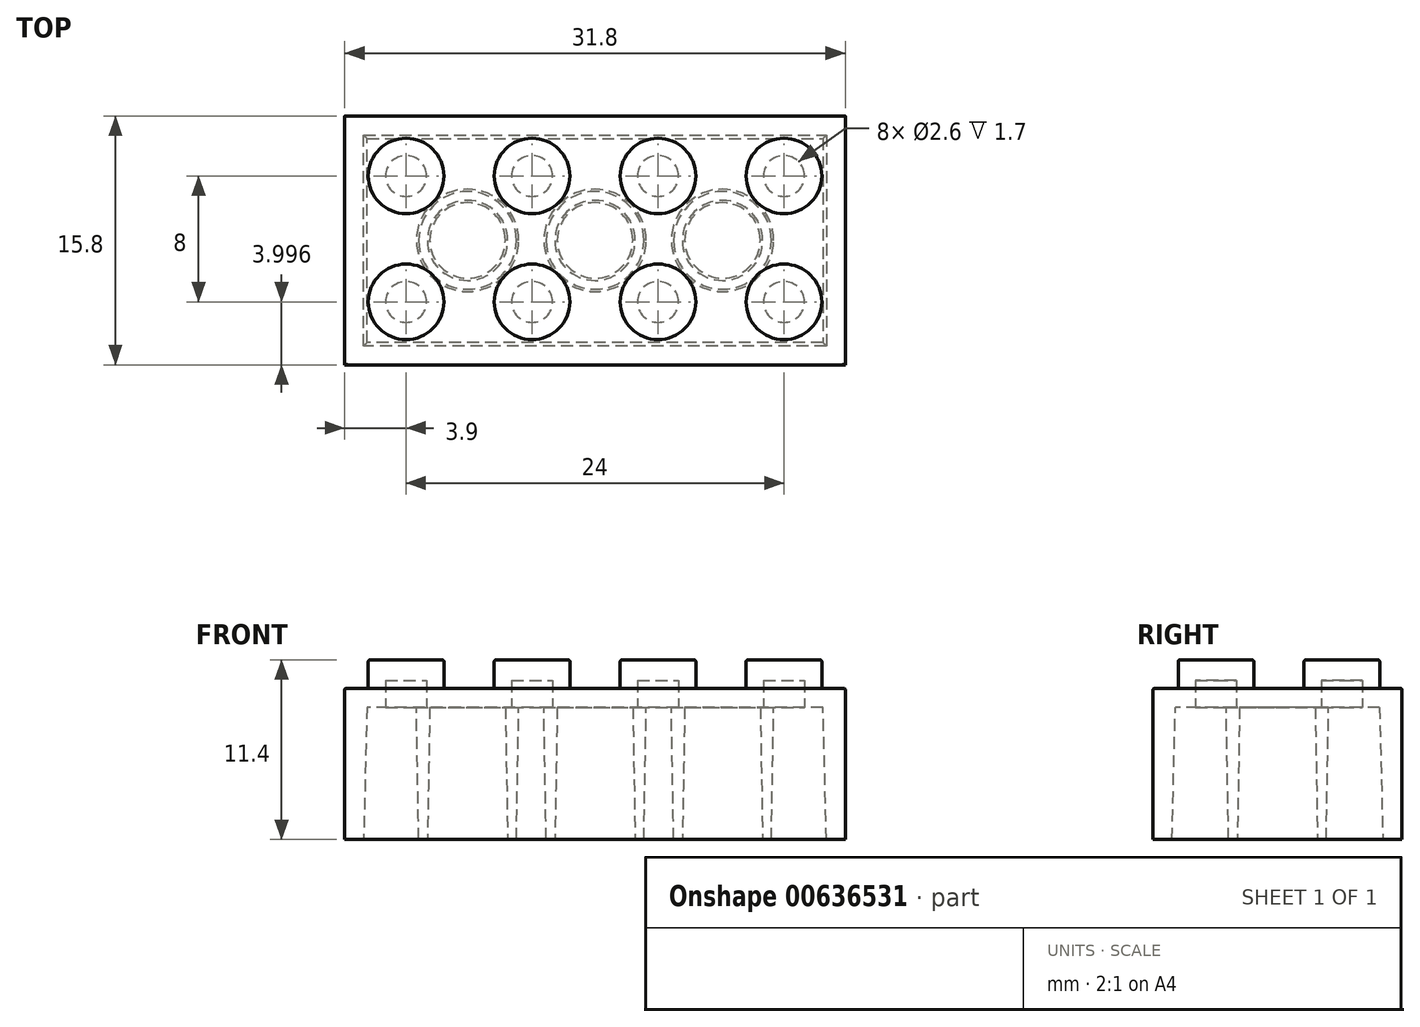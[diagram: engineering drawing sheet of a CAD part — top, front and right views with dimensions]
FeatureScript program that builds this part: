
annotation { "Feature Type Name" : "Feature", "Feature Type Description" : "" }
export const myFeature = defineFeature(function(context is Context, id is Id, definition is map)
    precondition{}
    {
        {
            var Q0;
            Q0=qCreatedBy(makeId("Top.planeOp"),FACE);
            var sketch = newSketch(context, id + "F0", { "sketchPlane" : qUnion([Q0])});
            skLineSegment(sketch, "E0.rect.bottom", {"start": v(15.9, -7.9) * mm, "end": v(-15.9, -7.9) * mm});
            skLineSegment(sketch, "E0.rect.top", {"start": v(15.9, 7.9) * mm, "end": v(-15.9, 7.9) * mm});
            skLineSegment(sketch, "E0.rect.left", {"start": v(15.9, -7.9) * mm, "end": v(15.9, 7.9) * mm});
            skLineSegment(sketch, "E0.rect.right", {"start": v(-15.9, -7.9) * mm, "end": v(-15.9, 7.9) * mm});
            skPoint(sketch, "E0.rect.middle", {"position": v(0, 0) * mm});
            skSolve(sketch);
        }
        {
            var Q0;
            Q0=makeQuery(id+"F0.imprint","IMPRINT",FACE,{"disambiguationData":[TD([[makeQuery(id+"F0.imprint","IMPRINT",EDGE,{"derivedFrom":sQuery(id+"F0.wireOp",EDGE,"E0.rect.bottom")}),-1.0]])]});
            extrude(context, id + "F1", {"entities" : qUnion([Q0]), "depth" : 9.6 * mm});
        }
        {
            var Q0;
            Q0=makeQuery(id+"F1.opExtrude","CAP_FACE",FACE,{"disambiguationData":[OSD([sQuery(id+"F0.wireOp",EDGE,"E0.rect.bottom"),sQuery(id+"F0.wireOp",EDGE,"E0.rect.top"),sQuery(id+"F0.wireOp",EDGE,"E0.rect.left"),sQuery(id+"F0.wireOp",EDGE,"E0.rect.right")])],"isStart":false});
            var sketch = newSketch(context, id + "F2", { "sketchPlane" : qUnion([Q0])});
            skCircle(sketch, "E1", {"center": v(12, -3.9) * mm, "radius": 2.4 * mm});
            skCircle(sketch, "E2.0.1.0", {"center": v(12, 4.1) * mm, "radius": 2.4 * mm});
            skCircle(sketch, "E2.1.0.0", {"center": v(4, -3.9) * mm, "radius": 2.4 * mm});
            skCircle(sketch, "E2.1.1.0", {"center": v(4, 4.1) * mm, "radius": 2.4 * mm});
            skCircle(sketch, "E2.2.0.0", {"center": v(-4, -3.9) * mm, "radius": 2.4 * mm});
            skCircle(sketch, "E2.2.1.0", {"center": v(-4, 4.1) * mm, "radius": 2.4 * mm});
            skCircle(sketch, "E2.3.0.0", {"center": v(-12, -3.9) * mm, "radius": 2.4 * mm});
            skCircle(sketch, "E2.3.1.0", {"center": v(-12, 4.1) * mm, "radius": 2.4 * mm});
            skLineSegment(sketch, "E2.direction1", {"start": v(12, -3.9) * mm, "end": v(4, -3.9) * mm, "construction": true});
            skLineSegment(sketch, "E2.direction2", {"start": v(12, -3.9) * mm, "end": v(12, 4.1) * mm, "construction": true});
            skSolve(sketch);
        }
        {
            var Q0;
            Q0=qSketchRegion(id+"F2",true);
            extrude(context, id + "F3", {"entities" : qUnion([Q0]), "operationType" : NewBodyOperationType.ADD, "depth" : 1.8 * mm});
        }
        {
            var Q0;
            Q0=makeQuery(id+"F1.opExtrude","CAP_FACE",FACE,{"disambiguationData":[OSD([sQuery(id+"F0.wireOp",EDGE,"E0.rect.bottom"),sQuery(id+"F0.wireOp",EDGE,"E0.rect.top"),sQuery(id+"F0.wireOp",EDGE,"E0.rect.left"),sQuery(id+"F0.wireOp",EDGE,"E0.rect.right")])],"isStart":true});
            var sketch = newSketch(context, id + "F4", { "sketchPlane" : qUnion([Q0])});
            skLineSegment(sketch, "E3.0", {"start": v(14.7, 6.7) * mm, "end": v(-14.7, 6.7) * mm});
            skLineSegment(sketch, "E3.1", {"start": v(14.7, 6.7) * mm, "end": v(14.7, -6.7) * mm});
            skLineSegment(sketch, "E3.2", {"start": v(14.7, -6.7) * mm, "end": v(-14.7, -6.7) * mm});
            skLineSegment(sketch, "E3.3", {"start": v(-14.7, 6.7) * mm, "end": v(-14.7, -6.7) * mm});
            skSolve(sketch);
        }
        {
            var Q0;
            Q0=qSketchRegion(id+"F4",true);
            extrude(context, id + "F5", {"entities" : qUnion([Q0]), "operationType" : NewBodyOperationType.REMOVE, "oppositeDirection" : true, "depth" : (9.6 - 1.2) * mm, "hasDraft" : true, "draftAngle" : 1.5 * degree, "draftPullDirection" : true});
        }
        {
            var Q0;
            Q0=makeQuery(id+"F5.boolean.opBoolean","COPY",FACE,{"derivedFrom":makeQuery(id+"F5.opExtrude","CAP_FACE",FACE,{"disambiguationData":[OSD([sQuery(id+"F4.wireOp",EDGE,"E3.0"),sQuery(id+"F4.wireOp",EDGE,"E3.1"),sQuery(id+"F4.wireOp",EDGE,"E3.2"),sQuery(id+"F4.wireOp",EDGE,"E3.3")])],"isStart":false})});
            var sketch = newSketch(context, id + "F6", { "sketchPlane" : qUnion([Q0])});
            skCircle(sketch, "E4.0", {"center": v(12, 3.9) * mm, "radius": 2.4 * mm, "construction": true});
            skCircle(sketch, "E5.0", {"center": v(4, 3.9) * mm, "radius": 2.4 * mm, "construction": true});
            skCircle(sketch, "E6.0", {"center": v(-4, 3.9) * mm, "radius": 2.4 * mm, "construction": true});
            skCircle(sketch, "E7.0", {"center": v(-12, 3.9) * mm, "radius": 2.4 * mm, "construction": true});
            skCircle(sketch, "E8.0", {"center": v(-12, -4.1) * mm, "radius": 2.4 * mm, "construction": true});
            skCircle(sketch, "E9.0", {"center": v(-4, -4.1) * mm, "radius": 2.4 * mm, "construction": true});
            skCircle(sketch, "E10.0", {"center": v(4, -4.1) * mm, "radius": 2.4 * mm, "construction": true});
            skCircle(sketch, "E11.0", {"center": v(12, -4.1) * mm, "radius": 2.4 * mm, "construction": true});
            skCircle(sketch, "E12", {"center": v(-12, 3.9) * mm, "radius": 1.3 * mm});
            skCircle(sketch, "E13", {"center": v(-4, 3.9) * mm, "radius": 1.3 * mm});
            skCircle(sketch, "E14", {"center": v(4, 3.9) * mm, "radius": 1.3 * mm});
            skCircle(sketch, "E15", {"center": v(12, 3.9) * mm, "radius": 1.3 * mm});
            skCircle(sketch, "E16", {"center": v(12, -4.1) * mm, "radius": 1.3 * mm});
            skCircle(sketch, "E17", {"center": v(4, -4.1) * mm, "radius": 1.3 * mm});
            skCircle(sketch, "E18", {"center": v(-4, -4.1) * mm, "radius": 1.3 * mm});
            skCircle(sketch, "E19", {"center": v(-12, -4.1) * mm, "radius": 1.3 * mm});
            skSolve(sketch);
        }
        {
            var Q0;
            Q0=qSketchRegion(id+"F6",true);
            extrude(context, id + "F7", {"entities" : qUnion([Q0]), "operationType" : NewBodyOperationType.REMOVE, "oppositeDirection" : true, "depth" : 1.7 * mm});
        }
        {
            var Q0;
            Q0=makeQuery(id+"F5.boolean.opBoolean","COPY",FACE,{"derivedFrom":makeQuery(id+"F5.opExtrude","CAP_FACE",FACE,{"disambiguationData":[OSD([sQuery(id+"F4.wireOp",EDGE,"E3.0"),sQuery(id+"F4.wireOp",EDGE,"E3.1"),sQuery(id+"F4.wireOp",EDGE,"E3.2"),sQuery(id+"F4.wireOp",EDGE,"E3.3")])],"isStart":false})});
            var sketch = newSketch(context, id + "F8", { "sketchPlane" : qUnion([Q0])});
            skLineSegment(sketch, "E20.0", {"start": v(-15.9, 7.9) * mm, "end": v(-15.9, -7.9) * mm, "construction": true});
            skLineSegment(sketch, "E21", {"start": v(-15.9, 0) * mm, "end": v(17.94, 0) * mm});
            skPoint(sketch, "E21.endSnap0", {"position": v(-15.9, 0) * mm});
            skCircle(sketch, "E22", {"center": v(0, 0) * mm, "radius": 3.25 * mm});
            skCircle(sketch, "E23", {"center": v(8.1, 0) * mm, "radius": 3.25 * mm});
            skCircle(sketch, "E24", {"center": v(-8.1, 0) * mm, "radius": 3.25 * mm});
            skCircle(sketch, "E25", {"center": v(-8.1, 0) * mm, "radius": 2.4 * mm});
            skCircle(sketch, "E26", {"center": v(0, 0) * mm, "radius": 2.4 * mm});
            skCircle(sketch, "E27", {"center": v(8.1, 0) * mm, "radius": 2.4 * mm});
            skLineSegment(sketch, "E28", {"start": v(-12, 3.9) * mm, "end": v(-4, -4.1) * mm, "construction": true});
            skSolve(sketch);
        }
        {
            var Q0;
            Q0=qSketchRegion(id+"F8",true);
            var Q1;
            Q1=makeQuery(id+"F1.opExtrude","CAP_FACE",FACE,{"disambiguationData":[OSD([sQuery(id+"F0.wireOp",EDGE,"E0.rect.bottom"),sQuery(id+"F0.wireOp",EDGE,"E0.rect.top"),sQuery(id+"F0.wireOp",EDGE,"E0.rect.left"),sQuery(id+"F0.wireOp",EDGE,"E0.rect.right")])],"isStart":true});
            extrude(context, id + "F9", {"entities" : qUnion([Q0]), "operationType" : NewBodyOperationType.ADD, "endBound" : BoundingType.UP_TO_SURFACE, "endBoundEntityFace" : qUnion([Q1]), "depth" : 25 * mm, "hasDraft" : true, "draftAngle" : 1 * degree, "draftPullDirection" : true});
        }
        {
            var Q0;
            Q0=makeQuery(id+"F3.opExtrude","CAP_EDGE",EDGE,{"disambiguationData":[OSD([sQuery(id+"F2.wireOp",EDGE,"E2.1.0.0")])],"isStart":false});
            var Q1;
            Q1=makeQuery(id+"F3.opExtrude","CAP_EDGE",EDGE,{"disambiguationData":[OSD([sQuery(id+"F2.wireOp",EDGE,"E2.3.0.0")])],"isStart":false});
            var Q2;
            Q2=makeQuery(id+"F3.opExtrude","CAP_EDGE",EDGE,{"disambiguationData":[OSD([sQuery(id+"F2.wireOp",EDGE,"E2.3.1.0")])],"isStart":false});
            var Q3;
            Q3=makeQuery(id+"F3.opExtrude","CAP_EDGE",EDGE,{"disambiguationData":[OSD([sQuery(id+"F2.wireOp",EDGE,"E2.2.1.0")])],"isStart":false});
            var Q4;
            Q4=makeQuery(id+"F3.opExtrude","CAP_EDGE",EDGE,{"disambiguationData":[OSD([sQuery(id+"F2.wireOp",EDGE,"E2.2.0.0")])],"isStart":false});
            var Q5;
            Q5=makeQuery(id+"F3.opExtrude","CAP_EDGE",EDGE,{"disambiguationData":[OSD([sQuery(id+"F2.wireOp",EDGE,"E2.1.1.0")])],"isStart":false});
            var Q6;
            Q6=makeQuery(id+"F3.opExtrude","CAP_EDGE",EDGE,{"disambiguationData":[OSD([sQuery(id+"F2.wireOp",EDGE,"E2.0.1.0")])],"isStart":false});
            var Q7;
            Q7=makeQuery(id+"F3.opExtrude","CAP_EDGE",EDGE,{"disambiguationData":[OSD([sQuery(id+"F2.wireOp",EDGE,"E1")])],"isStart":false});
            var Q8;
            Q8=makeQuery(id+"F1.opExtrude","CAP_EDGE",EDGE,{"disambiguationData":[OSD([sQuery(id+"F0.wireOp",EDGE,"E0.rect.left")])],"isStart":false});
            var Q9;
            Q9=makeQuery(id+"F1.opExtrude","CAP_EDGE",EDGE,{"disambiguationData":[OSD([sQuery(id+"F0.wireOp",EDGE,"E0.rect.top")])],"isStart":false});
            var Q10;
            Q10=makeQuery(id+"F1.opExtrude","CAP_EDGE",EDGE,{"disambiguationData":[OSD([sQuery(id+"F0.wireOp",EDGE,"E0.rect.right")])],"isStart":false});
            var Q11;
            Q11=makeQuery(id+"F1.opExtrude","CAP_EDGE",EDGE,{"disambiguationData":[OSD([sQuery(id+"F0.wireOp",EDGE,"E0.rect.bottom")])],"isStart":false});
            fillet(context, id + "F10", {"entities" : qUnion([Q0, Q1, Q2, Q3, Q4, Q5, Q6, Q7, Q8, Q9, Q10, Q11]), "radius" : .1 * mm, "tangentPropagation" : true, "allowEdgeOverflow" : false});
        }
    });
